annotation { "Feature Type Name" : "Feature", "Feature Type Description" : "" }
export const myFeature = defineFeature(function(context is Context, id is Id, definition is map)
    precondition{}
    {
        {
            var Q0;
            Q0=qCreatedBy(makeId("Top.planeOp"),FACE);
            var sketch = newSketch(context, id + "F0", { "sketchPlane" : qUnion([Q0])});
            skCircle(sketch, "E0", {"center": v(0, 0) * mm, "radius": 50000 * mm});
            skCircle(sketch, "E1", {"center": v(0, 0) * mm, "radius": 40000 * mm});
            skCircle(sketch, "E2", {"center": v(0, 0) * mm, "radius": 30000 * mm});
            skCircle(sketch, "E3", {"center": v(0, 0) * mm, "radius": 20000 * mm});
            skCircle(sketch, "E4", {"center": v(0, 0) * mm, "radius": 10000 * mm});
            skCircle(sketch, "E5", {"center": v(0, 0) * mm, "radius": 8000 * mm});
            skCircle(sketch, "E6", {"center": v(0, 0) * mm, "radius": 6000 * mm});
            skCircle(sketch, "E7", {"center": v(0, 0) * mm, "radius": 4000 * mm});
            skCircle(sketch, "E8", {"center": v(0, 0) * mm, "radius": 2000 * mm});
            skCircle(sketch, "E9.0", {"center": v(0, 0) * mm, "radius": 50100 * mm});
            skCircle(sketch, "E10.0", {"center": v(0, 0) * mm, "radius": 40100 * mm});
            skCircle(sketch, "E11.0", {"center": v(0, 0) * mm, "radius": 30100 * mm});
            skCircle(sketch, "E12.0", {"center": v(0, 0) * mm, "radius": 20100 * mm});
            skCircle(sketch, "E13.0", {"center": v(0, 0) * mm, "radius": 10100 * mm});
            skCircle(sketch, "E14.0", {"center": v(0, 0) * mm, "radius": 8100 * mm});
            skCircle(sketch, "E15.0", {"center": v(0, 0) * mm, "radius": 6100 * mm});
            skCircle(sketch, "E16.0", {"center": v(0, 0) * mm, "radius": 4100 * mm});
            skCircle(sketch, "E17.0", {"center": v(0, 0) * mm, "radius": 2100 * mm});
            skSolve(sketch);
        }
        {
            var Q0;
            Q0=makeQuery(id+"F0.imprint","IMPRINT",FACE,{"disambiguationData":[TD([[makeQuery(id+"F0.imprint","IMPRINT",EDGE,{"derivedFrom":sQuery(id+"F0.wireOp",EDGE,"E0")}),-1.0]])]});
            var Q1;
            Q1=makeQuery(id+"F0.imprint","IMPRINT",FACE,{"disambiguationData":[TD([[makeQuery(id+"F0.imprint","IMPRINT",EDGE,{"derivedFrom":sQuery(id+"F0.wireOp",EDGE,"E1")}),-1.0]])]});
            var Q2;
            Q2=makeQuery(id+"F0.imprint","IMPRINT",FACE,{"disambiguationData":[TD([[makeQuery(id+"F0.imprint","IMPRINT",EDGE,{"derivedFrom":sQuery(id+"F0.wireOp",EDGE,"E2")}),-1.0]])]});
            var Q3;
            Q3=makeQuery(id+"F0.imprint","IMPRINT",FACE,{"disambiguationData":[TD([[makeQuery(id+"F0.imprint","IMPRINT",EDGE,{"derivedFrom":sQuery(id+"F0.wireOp",EDGE,"E3")}),-1.0]])]});
            var Q4;
            Q4=makeQuery(id+"F0.imprint","IMPRINT",FACE,{"disambiguationData":[TD([[makeQuery(id+"F0.imprint","IMPRINT",EDGE,{"derivedFrom":sQuery(id+"F0.wireOp",EDGE,"E4")}),-1.0]])]});
            var Q5;
            Q5=makeQuery(id+"F0.imprint","IMPRINT",FACE,{"disambiguationData":[TD([[makeQuery(id+"F0.imprint","IMPRINT",EDGE,{"derivedFrom":sQuery(id+"F0.wireOp",EDGE,"E5")}),-1.0]])]});
            var Q6;
            Q6=makeQuery(id+"F0.imprint","IMPRINT",FACE,{"disambiguationData":[TD([[makeQuery(id+"F0.imprint","IMPRINT",EDGE,{"derivedFrom":sQuery(id+"F0.wireOp",EDGE,"E6")}),-1.0]])]});
            var Q7;
            Q7=makeQuery(id+"F0.imprint","IMPRINT",FACE,{"disambiguationData":[TD([[makeQuery(id+"F0.imprint","IMPRINT",EDGE,{"derivedFrom":sQuery(id+"F0.wireOp",EDGE,"E7")}),-1.0]])]});
            var Q8;
            Q8=makeQuery(id+"F0.imprint","IMPRINT",FACE,{"disambiguationData":[TD([[makeQuery(id+"F0.imprint","IMPRINT",EDGE,{"derivedFrom":sQuery(id+"F0.wireOp",EDGE,"E8")}),-1.0]])]});
            extrude(context, id + "F1", {"entities" : qUnion([Q0, Q1, Q2, Q3, Q4, Q5, Q6, Q7, Q8]), "depth" : 10 * mm});
        }
        {
            var Q0;
            Q0=qCreatedBy(makeId("Top.planeOp"),FACE);
            var sketch = newSketch(context, id + "F2", { "sketchPlane" : qUnion([Q0])});
            skLineSegment(sketch, "E18.bottom", {"start": v(-15000, 5000) * mm, "end": v(-60000, 5000) * mm});
            skLineSegment(sketch, "E18.top", {"start": v(-15000, -5000) * mm, "end": v(-60000, -5000) * mm});
            skLineSegment(sketch, "E18.left", {"start": v(-15000, 5000) * mm, "end": v(-15000, -5000) * mm});
            skLineSegment(sketch, "E18.right", {"start": v(-60000, 5000) * mm, "end": v(-60000, -5000) * mm});
            skSolve(sketch);
        }
        {
            var Q0;
            Q0=qSketchRegion(id+"F2",true);
            extrude(context, id + "F3", {"entities" : qUnion([Q0]), "operationType" : NewBodyOperationType.REMOVE, "endBound" : BoundingType.THROUGH_ALL, "depth" : 25 * mm});
        }
        {
            var Q0;
            Q0=qCreatedBy(makeId("Top.planeOp"),FACE);
            var sketch = newSketch(context, id + "F4", { "sketchPlane" : qUnion([Q0])});
            skText(sketch, "E19", { "text": "50m", "fontName": "OpenSans-Regular.ttf"});
            skText(sketch, "E20", { "text": "40m", "fontName": "OpenSans-Regular.ttf"});
            skText(sketch, "E21", { "text": "30m", "fontName": "OpenSans-Regular.ttf"});
            skText(sketch, "E22", { "text": "20m", "fontName": "OpenSans-Regular.ttf"});
            const initialGuessF4  = {"E19": [-52.85742, -1, 1, 0, 2], "E20": [-42.85742, -1, 1, 0, 2], "E21": [-32.85742, -1, 1, 0, 2], "E22": [-22.85742, -1, 1, 0, 2]};
            skSetInitialGuess(sketch, initialGuessF4);
            skSolve(sketch);
        }
        {
            var Q0;
            Q0=qSketchRegion(id+"F4",true);
            var Q1;
            Q1=makeQuery(id+"F1.opExtrude","CAP_FACE",FACE,{"disambiguationData":[OSD([sQuery(id+"F0.wireOp",EDGE,"E0"),sQuery(id+"F0.wireOp",EDGE,"E9.0")])],"isStart":false});
            var Q2;
            Q2=makeQuery(id+"F1.opExtrude","SWEPT_BODY",BODY,{"disambiguationData":[OSD([sQuery(id+"F0.wireOp",EDGE,"E0"),sQuery(id+"F0.wireOp",EDGE,"E9.0")])]});
            extrude(context, id + "F5", {"entities" : qUnion([Q0]), "endBound" : BoundingType.UP_TO_SURFACE, "endBoundEntityFace" : qUnion([Q1]), "endBoundEntityBody" : qUnion([Q2]), "depth" : 25 * mm});
        }
        {
            var Q0;
            Q0=qCreatedBy(makeId("Front.planeOp"),FACE);
            var sketch = newSketch(context, id + "F6", { "sketchPlane" : qUnion([Q0])});
            skLineSegment(sketch, "E23", {"start": v(0, 979.96) * mm, "end": v(0, 0) * mm});
            skLineSegment(sketch, "E24", {"start": v(0, 0) * mm, "end": v(1421.91, 0) * mm});
            skSolve(sketch);
        }
        {
            var Q0;
            Q0=makeQuery(id+"F5.opExtrude","SWEPT_BODY",BODY,{"disambiguationData":[OSD([sQuery(id+"F4.wireOp",EDGE,"E22.sketch_text.stroke-20"),sQuery(id+"F4.wireOp",EDGE,"E22.sketch_text.stroke-21"),sQuery(id+"F4.wireOp",EDGE,"E22.sketch_text.stroke-22"),sQuery(id+"F4.wireOp",EDGE,"E22.sketch_text.stroke-23"),sQuery(id+"F4.wireOp",EDGE,"E22.sketch_text.stroke-24"),sQuery(id+"F4.wireOp",EDGE,"E22.sketch_text.stroke-25"),sQuery(id+"F4.wireOp",EDGE,"E22.sketch_text.stroke-26"),sQuery(id+"F4.wireOp",EDGE,"E22.sketch_text.stroke-27"),sQuery(id+"F4.wireOp",EDGE,"E22.sketch_text.stroke-28"),sQuery(id+"F4.wireOp",EDGE,"E22.sketch_text.stroke-29"),sQuery(id+"F4.wireOp",EDGE,"E22.sketch_text.stroke-30"),sQuery(id+"F4.wireOp",EDGE,"E22.sketch_text.stroke-31"),sQuery(id+"F4.wireOp",EDGE,"E22.sketch_text.stroke-32"),sQuery(id+"F4.wireOp",EDGE,"E22.sketch_text.stroke-33"),sQuery(id+"F4.wireOp",EDGE,"E22.sketch_text.stroke-34"),sQuery(id+"F4.wireOp",EDGE,"E22.sketch_text.stroke-35")])]});
            var Q1;
            Q1=makeQuery(id+"F5.opExtrude","SWEPT_BODY",BODY,{"disambiguationData":[OSD([sQuery(id+"F4.wireOp",EDGE,"E22.sketch_text.stroke-0"),sQuery(id+"F4.wireOp",EDGE,"E22.sketch_text.stroke-1"),sQuery(id+"F4.wireOp",EDGE,"E22.sketch_text.stroke-2"),sQuery(id+"F4.wireOp",EDGE,"E22.sketch_text.stroke-3"),sQuery(id+"F4.wireOp",EDGE,"E22.sketch_text.stroke-4"),sQuery(id+"F4.wireOp",EDGE,"E22.sketch_text.stroke-5"),sQuery(id+"F4.wireOp",EDGE,"E22.sketch_text.stroke-6"),sQuery(id+"F4.wireOp",EDGE,"E22.sketch_text.stroke-7"),sQuery(id+"F4.wireOp",EDGE,"E22.sketch_text.stroke-8"),sQuery(id+"F4.wireOp",EDGE,"E22.sketch_text.stroke-9"),sQuery(id+"F4.wireOp",EDGE,"E22.sketch_text.stroke-10"),sQuery(id+"F4.wireOp",EDGE,"E22.sketch_text.stroke-11"),sQuery(id+"F4.wireOp",EDGE,"E22.sketch_text.stroke-12"),sQuery(id+"F4.wireOp",EDGE,"E22.sketch_text.stroke-13"),sQuery(id+"F4.wireOp",EDGE,"E22.sketch_text.stroke-14"),sQuery(id+"F4.wireOp",EDGE,"E22.sketch_text.stroke-15"),sQuery(id+"F4.wireOp",EDGE,"E22.sketch_text.stroke-16"),sQuery(id+"F4.wireOp",EDGE,"E22.sketch_text.stroke-17"),sQuery(id+"F4.wireOp",EDGE,"E22.sketch_text.stroke-18"),sQuery(id+"F4.wireOp",EDGE,"E22.sketch_text.stroke-19")])]});
            var Q2;
            Q2=makeQuery(id+"F5.opExtrude","SWEPT_BODY",BODY,{"disambiguationData":[OSD([sQuery(id+"F4.wireOp",EDGE,"E21.sketch_text.stroke-28"),sQuery(id+"F4.wireOp",EDGE,"E21.sketch_text.stroke-29"),sQuery(id+"F4.wireOp",EDGE,"E21.sketch_text.stroke-30"),sQuery(id+"F4.wireOp",EDGE,"E21.sketch_text.stroke-31"),sQuery(id+"F4.wireOp",EDGE,"E21.sketch_text.stroke-32"),sQuery(id+"F4.wireOp",EDGE,"E21.sketch_text.stroke-33"),sQuery(id+"F4.wireOp",EDGE,"E21.sketch_text.stroke-34"),sQuery(id+"F4.wireOp",EDGE,"E21.sketch_text.stroke-35"),sQuery(id+"F4.wireOp",EDGE,"E21.sketch_text.stroke-36"),sQuery(id+"F4.wireOp",EDGE,"E21.sketch_text.stroke-37"),sQuery(id+"F4.wireOp",EDGE,"E21.sketch_text.stroke-38"),sQuery(id+"F4.wireOp",EDGE,"E21.sketch_text.stroke-39"),sQuery(id+"F4.wireOp",EDGE,"E21.sketch_text.stroke-40"),sQuery(id+"F4.wireOp",EDGE,"E21.sketch_text.stroke-41"),sQuery(id+"F4.wireOp",EDGE,"E21.sketch_text.stroke-42"),sQuery(id+"F4.wireOp",EDGE,"E21.sketch_text.stroke-43")])]});
            var Q3;
            Q3=makeQuery(id+"F5.opExtrude","SWEPT_BODY",BODY,{"disambiguationData":[OSD([sQuery(id+"F4.wireOp",EDGE,"E21.sketch_text.stroke-0"),sQuery(id+"F4.wireOp",EDGE,"E21.sketch_text.stroke-1"),sQuery(id+"F4.wireOp",EDGE,"E21.sketch_text.stroke-2"),sQuery(id+"F4.wireOp",EDGE,"E21.sketch_text.stroke-3"),sQuery(id+"F4.wireOp",EDGE,"E21.sketch_text.stroke-4"),sQuery(id+"F4.wireOp",EDGE,"E21.sketch_text.stroke-5"),sQuery(id+"F4.wireOp",EDGE,"E21.sketch_text.stroke-6"),sQuery(id+"F4.wireOp",EDGE,"E21.sketch_text.stroke-7"),sQuery(id+"F4.wireOp",EDGE,"E21.sketch_text.stroke-8"),sQuery(id+"F4.wireOp",EDGE,"E21.sketch_text.stroke-9"),sQuery(id+"F4.wireOp",EDGE,"E21.sketch_text.stroke-10"),sQuery(id+"F4.wireOp",EDGE,"E21.sketch_text.stroke-11"),sQuery(id+"F4.wireOp",EDGE,"E21.sketch_text.stroke-12"),sQuery(id+"F4.wireOp",EDGE,"E21.sketch_text.stroke-13"),sQuery(id+"F4.wireOp",EDGE,"E21.sketch_text.stroke-14"),sQuery(id+"F4.wireOp",EDGE,"E21.sketch_text.stroke-15"),sQuery(id+"F4.wireOp",EDGE,"E21.sketch_text.stroke-16"),sQuery(id+"F4.wireOp",EDGE,"E21.sketch_text.stroke-17"),sQuery(id+"F4.wireOp",EDGE,"E21.sketch_text.stroke-18"),sQuery(id+"F4.wireOp",EDGE,"E21.sketch_text.stroke-19"),sQuery(id+"F4.wireOp",EDGE,"E21.sketch_text.stroke-20"),sQuery(id+"F4.wireOp",EDGE,"E21.sketch_text.stroke-21"),sQuery(id+"F4.wireOp",EDGE,"E21.sketch_text.stroke-22"),sQuery(id+"F4.wireOp",EDGE,"E21.sketch_text.stroke-23"),sQuery(id+"F4.wireOp",EDGE,"E21.sketch_text.stroke-24"),sQuery(id+"F4.wireOp",EDGE,"E21.sketch_text.stroke-25"),sQuery(id+"F4.wireOp",EDGE,"E21.sketch_text.stroke-26"),sQuery(id+"F4.wireOp",EDGE,"E21.sketch_text.stroke-27")])]});
            var Q4;
            Q4=makeQuery(id+"F5.opExtrude","SWEPT_BODY",BODY,{"disambiguationData":[OSD([sQuery(id+"F4.wireOp",EDGE,"E20.sketch_text.stroke-17"),sQuery(id+"F4.wireOp",EDGE,"E20.sketch_text.stroke-18"),sQuery(id+"F4.wireOp",EDGE,"E20.sketch_text.stroke-19"),sQuery(id+"F4.wireOp",EDGE,"E20.sketch_text.stroke-20"),sQuery(id+"F4.wireOp",EDGE,"E20.sketch_text.stroke-21"),sQuery(id+"F4.wireOp",EDGE,"E20.sketch_text.stroke-22"),sQuery(id+"F4.wireOp",EDGE,"E20.sketch_text.stroke-23"),sQuery(id+"F4.wireOp",EDGE,"E20.sketch_text.stroke-24"),sQuery(id+"F4.wireOp",EDGE,"E20.sketch_text.stroke-25"),sQuery(id+"F4.wireOp",EDGE,"E20.sketch_text.stroke-26"),sQuery(id+"F4.wireOp",EDGE,"E20.sketch_text.stroke-27"),sQuery(id+"F4.wireOp",EDGE,"E20.sketch_text.stroke-28"),sQuery(id+"F4.wireOp",EDGE,"E20.sketch_text.stroke-29"),sQuery(id+"F4.wireOp",EDGE,"E20.sketch_text.stroke-30"),sQuery(id+"F4.wireOp",EDGE,"E20.sketch_text.stroke-31"),sQuery(id+"F4.wireOp",EDGE,"E20.sketch_text.stroke-32")])]});
            var Q5;
            Q5=makeQuery(id+"F5.opExtrude","SWEPT_BODY",BODY,{"disambiguationData":[OSD([sQuery(id+"F4.wireOp",EDGE,"E20.sketch_text.stroke-0"),sQuery(id+"F4.wireOp",EDGE,"E20.sketch_text.stroke-1"),sQuery(id+"F4.wireOp",EDGE,"E20.sketch_text.stroke-2"),sQuery(id+"F4.wireOp",EDGE,"E20.sketch_text.stroke-3"),sQuery(id+"F4.wireOp",EDGE,"E20.sketch_text.stroke-4"),sQuery(id+"F4.wireOp",EDGE,"E20.sketch_text.stroke-5"),sQuery(id+"F4.wireOp",EDGE,"E20.sketch_text.stroke-6"),sQuery(id+"F4.wireOp",EDGE,"E20.sketch_text.stroke-7"),sQuery(id+"F4.wireOp",EDGE,"E20.sketch_text.stroke-8"),sQuery(id+"F4.wireOp",EDGE,"E20.sketch_text.stroke-9"),sQuery(id+"F4.wireOp",EDGE,"E20.sketch_text.stroke-10"),sQuery(id+"F4.wireOp",EDGE,"E20.sketch_text.stroke-11"),sQuery(id+"F4.wireOp",EDGE,"E20.sketch_text.stroke-12"),sQuery(id+"F4.wireOp",EDGE,"E20.sketch_text.stroke-13"),sQuery(id+"F4.wireOp",EDGE,"E20.sketch_text.stroke-14"),sQuery(id+"F4.wireOp",EDGE,"E20.sketch_text.stroke-15"),sQuery(id+"F4.wireOp",EDGE,"E20.sketch_text.stroke-16")])]});
            var Q6;
            Q6=makeQuery(id+"F5.opExtrude","SWEPT_BODY",BODY,{"disambiguationData":[OSD([sQuery(id+"F4.wireOp",EDGE,"E19.sketch_text.stroke-19"),sQuery(id+"F4.wireOp",EDGE,"E19.sketch_text.stroke-20"),sQuery(id+"F4.wireOp",EDGE,"E19.sketch_text.stroke-21"),sQuery(id+"F4.wireOp",EDGE,"E19.sketch_text.stroke-22"),sQuery(id+"F4.wireOp",EDGE,"E19.sketch_text.stroke-23"),sQuery(id+"F4.wireOp",EDGE,"E19.sketch_text.stroke-24"),sQuery(id+"F4.wireOp",EDGE,"E19.sketch_text.stroke-25"),sQuery(id+"F4.wireOp",EDGE,"E19.sketch_text.stroke-26"),sQuery(id+"F4.wireOp",EDGE,"E19.sketch_text.stroke-27"),sQuery(id+"F4.wireOp",EDGE,"E19.sketch_text.stroke-28"),sQuery(id+"F4.wireOp",EDGE,"E19.sketch_text.stroke-29"),sQuery(id+"F4.wireOp",EDGE,"E19.sketch_text.stroke-30"),sQuery(id+"F4.wireOp",EDGE,"E19.sketch_text.stroke-31"),sQuery(id+"F4.wireOp",EDGE,"E19.sketch_text.stroke-32"),sQuery(id+"F4.wireOp",EDGE,"E19.sketch_text.stroke-33"),sQuery(id+"F4.wireOp",EDGE,"E19.sketch_text.stroke-34")])]});
            var Q7;
            Q7=makeQuery(id+"F5.opExtrude","SWEPT_BODY",BODY,{"disambiguationData":[OSD([sQuery(id+"F4.wireOp",EDGE,"E19.sketch_text.stroke-0"),sQuery(id+"F4.wireOp",EDGE,"E19.sketch_text.stroke-1"),sQuery(id+"F4.wireOp",EDGE,"E19.sketch_text.stroke-2"),sQuery(id+"F4.wireOp",EDGE,"E19.sketch_text.stroke-3"),sQuery(id+"F4.wireOp",EDGE,"E19.sketch_text.stroke-4"),sQuery(id+"F4.wireOp",EDGE,"E19.sketch_text.stroke-5"),sQuery(id+"F4.wireOp",EDGE,"E19.sketch_text.stroke-6"),sQuery(id+"F4.wireOp",EDGE,"E19.sketch_text.stroke-7"),sQuery(id+"F4.wireOp",EDGE,"E19.sketch_text.stroke-8"),sQuery(id+"F4.wireOp",EDGE,"E19.sketch_text.stroke-9"),sQuery(id+"F4.wireOp",EDGE,"E19.sketch_text.stroke-10"),sQuery(id+"F4.wireOp",EDGE,"E19.sketch_text.stroke-11"),sQuery(id+"F4.wireOp",EDGE,"E19.sketch_text.stroke-12"),sQuery(id+"F4.wireOp",EDGE,"E19.sketch_text.stroke-13"),sQuery(id+"F4.wireOp",EDGE,"E19.sketch_text.stroke-14"),sQuery(id+"F4.wireOp",EDGE,"E19.sketch_text.stroke-15"),sQuery(id+"F4.wireOp",EDGE,"E19.sketch_text.stroke-16"),sQuery(id+"F4.wireOp",EDGE,"E19.sketch_text.stroke-17"),sQuery(id+"F4.wireOp",EDGE,"E19.sketch_text.stroke-18")])]});
            var Q8;
            Q8=makeQuery(id+"F5.opExtrude","SWEPT_BODY",BODY,{"disambiguationData":[OSD([sQuery(id+"F4.wireOp",EDGE,"E22.sketch_text.stroke-36"),sQuery(id+"F4.wireOp",EDGE,"E22.sketch_text.stroke-37"),sQuery(id+"F4.wireOp",EDGE,"E22.sketch_text.stroke-38"),sQuery(id+"F4.wireOp",EDGE,"E22.sketch_text.stroke-39"),sQuery(id+"F4.wireOp",EDGE,"E22.sketch_text.stroke-40"),sQuery(id+"F4.wireOp",EDGE,"E22.sketch_text.stroke-41"),sQuery(id+"F4.wireOp",EDGE,"E22.sketch_text.stroke-42"),sQuery(id+"F4.wireOp",EDGE,"E22.sketch_text.stroke-43"),sQuery(id+"F4.wireOp",EDGE,"E22.sketch_text.stroke-44"),sQuery(id+"F4.wireOp",EDGE,"E22.sketch_text.stroke-45"),sQuery(id+"F4.wireOp",EDGE,"E22.sketch_text.stroke-46"),sQuery(id+"F4.wireOp",EDGE,"E22.sketch_text.stroke-47"),sQuery(id+"F4.wireOp",EDGE,"E22.sketch_text.stroke-48"),sQuery(id+"F4.wireOp",EDGE,"E22.sketch_text.stroke-49"),sQuery(id+"F4.wireOp",EDGE,"E22.sketch_text.stroke-50"),sQuery(id+"F4.wireOp",EDGE,"E22.sketch_text.stroke-51"),sQuery(id+"F4.wireOp",EDGE,"E22.sketch_text.stroke-52"),sQuery(id+"F4.wireOp",EDGE,"E22.sketch_text.stroke-53"),sQuery(id+"F4.wireOp",EDGE,"E22.sketch_text.stroke-54"),sQuery(id+"F4.wireOp",EDGE,"E22.sketch_text.stroke-55"),sQuery(id+"F4.wireOp",EDGE,"E22.sketch_text.stroke-56"),sQuery(id+"F4.wireOp",EDGE,"E22.sketch_text.stroke-57"),sQuery(id+"F4.wireOp",EDGE,"E22.sketch_text.stroke-58"),sQuery(id+"F4.wireOp",EDGE,"E22.sketch_text.stroke-59"),sQuery(id+"F4.wireOp",EDGE,"E22.sketch_text.stroke-60"),sQuery(id+"F4.wireOp",EDGE,"E22.sketch_text.stroke-61"),sQuery(id+"F4.wireOp",EDGE,"E22.sketch_text.stroke-62"),sQuery(id+"F4.wireOp",EDGE,"E22.sketch_text.stroke-63")])]});
            var Q9;
            Q9=makeQuery(id+"F5.opExtrude","SWEPT_BODY",BODY,{"disambiguationData":[OSD([sQuery(id+"F4.wireOp",EDGE,"E21.sketch_text.stroke-44"),sQuery(id+"F4.wireOp",EDGE,"E21.sketch_text.stroke-45"),sQuery(id+"F4.wireOp",EDGE,"E21.sketch_text.stroke-46"),sQuery(id+"F4.wireOp",EDGE,"E21.sketch_text.stroke-47"),sQuery(id+"F4.wireOp",EDGE,"E21.sketch_text.stroke-48"),sQuery(id+"F4.wireOp",EDGE,"E21.sketch_text.stroke-49"),sQuery(id+"F4.wireOp",EDGE,"E21.sketch_text.stroke-50"),sQuery(id+"F4.wireOp",EDGE,"E21.sketch_text.stroke-51"),sQuery(id+"F4.wireOp",EDGE,"E21.sketch_text.stroke-52"),sQuery(id+"F4.wireOp",EDGE,"E21.sketch_text.stroke-53"),sQuery(id+"F4.wireOp",EDGE,"E21.sketch_text.stroke-54"),sQuery(id+"F4.wireOp",EDGE,"E21.sketch_text.stroke-55"),sQuery(id+"F4.wireOp",EDGE,"E21.sketch_text.stroke-56"),sQuery(id+"F4.wireOp",EDGE,"E21.sketch_text.stroke-57"),sQuery(id+"F4.wireOp",EDGE,"E21.sketch_text.stroke-58"),sQuery(id+"F4.wireOp",EDGE,"E21.sketch_text.stroke-59"),sQuery(id+"F4.wireOp",EDGE,"E21.sketch_text.stroke-60"),sQuery(id+"F4.wireOp",EDGE,"E21.sketch_text.stroke-61"),sQuery(id+"F4.wireOp",EDGE,"E21.sketch_text.stroke-62"),sQuery(id+"F4.wireOp",EDGE,"E21.sketch_text.stroke-63"),sQuery(id+"F4.wireOp",EDGE,"E21.sketch_text.stroke-64"),sQuery(id+"F4.wireOp",EDGE,"E21.sketch_text.stroke-65"),sQuery(id+"F4.wireOp",EDGE,"E21.sketch_text.stroke-66"),sQuery(id+"F4.wireOp",EDGE,"E21.sketch_text.stroke-67"),sQuery(id+"F4.wireOp",EDGE,"E21.sketch_text.stroke-68"),sQuery(id+"F4.wireOp",EDGE,"E21.sketch_text.stroke-69"),sQuery(id+"F4.wireOp",EDGE,"E21.sketch_text.stroke-70"),sQuery(id+"F4.wireOp",EDGE,"E21.sketch_text.stroke-71")])]});
            var Q10;
            Q10=makeQuery(id+"F5.opExtrude","SWEPT_BODY",BODY,{"disambiguationData":[OSD([sQuery(id+"F4.wireOp",EDGE,"E20.sketch_text.stroke-33"),sQuery(id+"F4.wireOp",EDGE,"E20.sketch_text.stroke-34"),sQuery(id+"F4.wireOp",EDGE,"E20.sketch_text.stroke-35"),sQuery(id+"F4.wireOp",EDGE,"E20.sketch_text.stroke-36"),sQuery(id+"F4.wireOp",EDGE,"E20.sketch_text.stroke-37"),sQuery(id+"F4.wireOp",EDGE,"E20.sketch_text.stroke-38"),sQuery(id+"F4.wireOp",EDGE,"E20.sketch_text.stroke-39"),sQuery(id+"F4.wireOp",EDGE,"E20.sketch_text.stroke-40"),sQuery(id+"F4.wireOp",EDGE,"E20.sketch_text.stroke-41"),sQuery(id+"F4.wireOp",EDGE,"E20.sketch_text.stroke-42"),sQuery(id+"F4.wireOp",EDGE,"E20.sketch_text.stroke-43"),sQuery(id+"F4.wireOp",EDGE,"E20.sketch_text.stroke-44"),sQuery(id+"F4.wireOp",EDGE,"E20.sketch_text.stroke-45"),sQuery(id+"F4.wireOp",EDGE,"E20.sketch_text.stroke-46"),sQuery(id+"F4.wireOp",EDGE,"E20.sketch_text.stroke-47"),sQuery(id+"F4.wireOp",EDGE,"E20.sketch_text.stroke-48"),sQuery(id+"F4.wireOp",EDGE,"E20.sketch_text.stroke-49"),sQuery(id+"F4.wireOp",EDGE,"E20.sketch_text.stroke-50"),sQuery(id+"F4.wireOp",EDGE,"E20.sketch_text.stroke-51"),sQuery(id+"F4.wireOp",EDGE,"E20.sketch_text.stroke-52"),sQuery(id+"F4.wireOp",EDGE,"E20.sketch_text.stroke-53"),sQuery(id+"F4.wireOp",EDGE,"E20.sketch_text.stroke-54"),sQuery(id+"F4.wireOp",EDGE,"E20.sketch_text.stroke-55"),sQuery(id+"F4.wireOp",EDGE,"E20.sketch_text.stroke-56"),sQuery(id+"F4.wireOp",EDGE,"E20.sketch_text.stroke-57"),sQuery(id+"F4.wireOp",EDGE,"E20.sketch_text.stroke-58"),sQuery(id+"F4.wireOp",EDGE,"E20.sketch_text.stroke-59"),sQuery(id+"F4.wireOp",EDGE,"E20.sketch_text.stroke-60")])]});
            var Q11;
            Q11=makeQuery(id+"F5.opExtrude","SWEPT_BODY",BODY,{"disambiguationData":[OSD([sQuery(id+"F4.wireOp",EDGE,"E19.sketch_text.stroke-35"),sQuery(id+"F4.wireOp",EDGE,"E19.sketch_text.stroke-36"),sQuery(id+"F4.wireOp",EDGE,"E19.sketch_text.stroke-37"),sQuery(id+"F4.wireOp",EDGE,"E19.sketch_text.stroke-38"),sQuery(id+"F4.wireOp",EDGE,"E19.sketch_text.stroke-39"),sQuery(id+"F4.wireOp",EDGE,"E19.sketch_text.stroke-40"),sQuery(id+"F4.wireOp",EDGE,"E19.sketch_text.stroke-41"),sQuery(id+"F4.wireOp",EDGE,"E19.sketch_text.stroke-42"),sQuery(id+"F4.wireOp",EDGE,"E19.sketch_text.stroke-43"),sQuery(id+"F4.wireOp",EDGE,"E19.sketch_text.stroke-44"),sQuery(id+"F4.wireOp",EDGE,"E19.sketch_text.stroke-45"),sQuery(id+"F4.wireOp",EDGE,"E19.sketch_text.stroke-46"),sQuery(id+"F4.wireOp",EDGE,"E19.sketch_text.stroke-47"),sQuery(id+"F4.wireOp",EDGE,"E19.sketch_text.stroke-48"),sQuery(id+"F4.wireOp",EDGE,"E19.sketch_text.stroke-49"),sQuery(id+"F4.wireOp",EDGE,"E19.sketch_text.stroke-50"),sQuery(id+"F4.wireOp",EDGE,"E19.sketch_text.stroke-51"),sQuery(id+"F4.wireOp",EDGE,"E19.sketch_text.stroke-52"),sQuery(id+"F4.wireOp",EDGE,"E19.sketch_text.stroke-53"),sQuery(id+"F4.wireOp",EDGE,"E19.sketch_text.stroke-54"),sQuery(id+"F4.wireOp",EDGE,"E19.sketch_text.stroke-55"),sQuery(id+"F4.wireOp",EDGE,"E19.sketch_text.stroke-56"),sQuery(id+"F4.wireOp",EDGE,"E19.sketch_text.stroke-57"),sQuery(id+"F4.wireOp",EDGE,"E19.sketch_text.stroke-58"),sQuery(id+"F4.wireOp",EDGE,"E19.sketch_text.stroke-59"),sQuery(id+"F4.wireOp",EDGE,"E19.sketch_text.stroke-60"),sQuery(id+"F4.wireOp",EDGE,"E19.sketch_text.stroke-61"),sQuery(id+"F4.wireOp",EDGE,"E19.sketch_text.stroke-62")])]});
            var Q12;
            Q12=sQuery(id+"F6.wireOp",EDGE,"E24");
            transform(context, id + "F7", {"entities" : qUnion([Q0, Q1, Q2, Q3, Q4, Q5, Q6, Q7, Q8, Q9, Q10, Q11]), "transformType" : TransformType.ROTATION, "transformAxis" : qUnion([Q12]), "angle" : 90 * degree, "makeCopy" : false});
        }
        {
            var Q0;
            Q0=makeQuery(id+"F1.opExtrude","SWEPT_BODY",BODY,{"disambiguationData":[OSD([sQuery(id+"F0.wireOp",EDGE,"E8"),sQuery(id+"F0.wireOp",EDGE,"E17.0")])]});
            var Q1;
            Q1=makeQuery(id+"F1.opExtrude","SWEPT_BODY",BODY,{"disambiguationData":[OSD([sQuery(id+"F0.wireOp",EDGE,"E7"),sQuery(id+"F0.wireOp",EDGE,"E16.0")])]});
            var Q2;
            Q2=makeQuery(id+"F1.opExtrude","SWEPT_BODY",BODY,{"disambiguationData":[OSD([sQuery(id+"F0.wireOp",EDGE,"E6"),sQuery(id+"F0.wireOp",EDGE,"E15.0")])]});
            var Q3;
            Q3=makeQuery(id+"F1.opExtrude","SWEPT_BODY",BODY,{"disambiguationData":[OSD([sQuery(id+"F0.wireOp",EDGE,"E5"),sQuery(id+"F0.wireOp",EDGE,"E14.0")])]});
            var Q4;
            Q4=makeQuery(id+"F1.opExtrude","SWEPT_BODY",BODY,{"disambiguationData":[OSD([sQuery(id+"F0.wireOp",EDGE,"E4"),sQuery(id+"F0.wireOp",EDGE,"E13.0")])]});
            var Q5;
            Q5=makeQuery(id+"F1.opExtrude","SWEPT_BODY",BODY,{"disambiguationData":[OSD([sQuery(id+"F0.wireOp",EDGE,"E3"),sQuery(id+"F0.wireOp",EDGE,"E12.0")])]});
            var Q6;
            Q6=makeQuery(id+"F1.opExtrude","SWEPT_BODY",BODY,{"disambiguationData":[OSD([sQuery(id+"F0.wireOp",EDGE,"E2"),sQuery(id+"F0.wireOp",EDGE,"E11.0")])]});
            var Q7;
            Q7=makeQuery(id+"F1.opExtrude","SWEPT_BODY",BODY,{"disambiguationData":[OSD([sQuery(id+"F0.wireOp",EDGE,"E1"),sQuery(id+"F0.wireOp",EDGE,"E10.0")])]});
            var Q8;
            Q8=makeQuery(id+"F1.opExtrude","SWEPT_BODY",BODY,{"disambiguationData":[OSD([sQuery(id+"F0.wireOp",EDGE,"E0"),sQuery(id+"F0.wireOp",EDGE,"E9.0")])]});
            var Q9;
            Q9=makeQuery(id+"F5.opExtrude","SWEPT_BODY",BODY,{"disambiguationData":[OSD([sQuery(id+"F4.wireOp",EDGE,"E22.sketch_text.stroke-20"),sQuery(id+"F4.wireOp",EDGE,"E22.sketch_text.stroke-21"),sQuery(id+"F4.wireOp",EDGE,"E22.sketch_text.stroke-22"),sQuery(id+"F4.wireOp",EDGE,"E22.sketch_text.stroke-23"),sQuery(id+"F4.wireOp",EDGE,"E22.sketch_text.stroke-24"),sQuery(id+"F4.wireOp",EDGE,"E22.sketch_text.stroke-25"),sQuery(id+"F4.wireOp",EDGE,"E22.sketch_text.stroke-26"),sQuery(id+"F4.wireOp",EDGE,"E22.sketch_text.stroke-27"),sQuery(id+"F4.wireOp",EDGE,"E22.sketch_text.stroke-28"),sQuery(id+"F4.wireOp",EDGE,"E22.sketch_text.stroke-29"),sQuery(id+"F4.wireOp",EDGE,"E22.sketch_text.stroke-30"),sQuery(id+"F4.wireOp",EDGE,"E22.sketch_text.stroke-31"),sQuery(id+"F4.wireOp",EDGE,"E22.sketch_text.stroke-32"),sQuery(id+"F4.wireOp",EDGE,"E22.sketch_text.stroke-33"),sQuery(id+"F4.wireOp",EDGE,"E22.sketch_text.stroke-34"),sQuery(id+"F4.wireOp",EDGE,"E22.sketch_text.stroke-35")])]});
            var Q10;
            Q10=makeQuery(id+"F5.opExtrude","SWEPT_BODY",BODY,{"disambiguationData":[OSD([sQuery(id+"F4.wireOp",EDGE,"E22.sketch_text.stroke-0"),sQuery(id+"F4.wireOp",EDGE,"E22.sketch_text.stroke-1"),sQuery(id+"F4.wireOp",EDGE,"E22.sketch_text.stroke-2"),sQuery(id+"F4.wireOp",EDGE,"E22.sketch_text.stroke-3"),sQuery(id+"F4.wireOp",EDGE,"E22.sketch_text.stroke-4"),sQuery(id+"F4.wireOp",EDGE,"E22.sketch_text.stroke-5"),sQuery(id+"F4.wireOp",EDGE,"E22.sketch_text.stroke-6"),sQuery(id+"F4.wireOp",EDGE,"E22.sketch_text.stroke-7"),sQuery(id+"F4.wireOp",EDGE,"E22.sketch_text.stroke-8"),sQuery(id+"F4.wireOp",EDGE,"E22.sketch_text.stroke-9"),sQuery(id+"F4.wireOp",EDGE,"E22.sketch_text.stroke-10"),sQuery(id+"F4.wireOp",EDGE,"E22.sketch_text.stroke-11"),sQuery(id+"F4.wireOp",EDGE,"E22.sketch_text.stroke-12"),sQuery(id+"F4.wireOp",EDGE,"E22.sketch_text.stroke-13"),sQuery(id+"F4.wireOp",EDGE,"E22.sketch_text.stroke-14"),sQuery(id+"F4.wireOp",EDGE,"E22.sketch_text.stroke-15"),sQuery(id+"F4.wireOp",EDGE,"E22.sketch_text.stroke-16"),sQuery(id+"F4.wireOp",EDGE,"E22.sketch_text.stroke-17"),sQuery(id+"F4.wireOp",EDGE,"E22.sketch_text.stroke-18"),sQuery(id+"F4.wireOp",EDGE,"E22.sketch_text.stroke-19")])]});
            var Q11;
            Q11=makeQuery(id+"F5.opExtrude","SWEPT_BODY",BODY,{"disambiguationData":[OSD([sQuery(id+"F4.wireOp",EDGE,"E21.sketch_text.stroke-28"),sQuery(id+"F4.wireOp",EDGE,"E21.sketch_text.stroke-29"),sQuery(id+"F4.wireOp",EDGE,"E21.sketch_text.stroke-30"),sQuery(id+"F4.wireOp",EDGE,"E21.sketch_text.stroke-31"),sQuery(id+"F4.wireOp",EDGE,"E21.sketch_text.stroke-32"),sQuery(id+"F4.wireOp",EDGE,"E21.sketch_text.stroke-33"),sQuery(id+"F4.wireOp",EDGE,"E21.sketch_text.stroke-34"),sQuery(id+"F4.wireOp",EDGE,"E21.sketch_text.stroke-35"),sQuery(id+"F4.wireOp",EDGE,"E21.sketch_text.stroke-36"),sQuery(id+"F4.wireOp",EDGE,"E21.sketch_text.stroke-37"),sQuery(id+"F4.wireOp",EDGE,"E21.sketch_text.stroke-38"),sQuery(id+"F4.wireOp",EDGE,"E21.sketch_text.stroke-39"),sQuery(id+"F4.wireOp",EDGE,"E21.sketch_text.stroke-40"),sQuery(id+"F4.wireOp",EDGE,"E21.sketch_text.stroke-41"),sQuery(id+"F4.wireOp",EDGE,"E21.sketch_text.stroke-42"),sQuery(id+"F4.wireOp",EDGE,"E21.sketch_text.stroke-43")])]});
            var Q12;
            Q12=makeQuery(id+"F5.opExtrude","SWEPT_BODY",BODY,{"disambiguationData":[OSD([sQuery(id+"F4.wireOp",EDGE,"E21.sketch_text.stroke-0"),sQuery(id+"F4.wireOp",EDGE,"E21.sketch_text.stroke-1"),sQuery(id+"F4.wireOp",EDGE,"E21.sketch_text.stroke-2"),sQuery(id+"F4.wireOp",EDGE,"E21.sketch_text.stroke-3"),sQuery(id+"F4.wireOp",EDGE,"E21.sketch_text.stroke-4"),sQuery(id+"F4.wireOp",EDGE,"E21.sketch_text.stroke-5"),sQuery(id+"F4.wireOp",EDGE,"E21.sketch_text.stroke-6"),sQuery(id+"F4.wireOp",EDGE,"E21.sketch_text.stroke-7"),sQuery(id+"F4.wireOp",EDGE,"E21.sketch_text.stroke-8"),sQuery(id+"F4.wireOp",EDGE,"E21.sketch_text.stroke-9"),sQuery(id+"F4.wireOp",EDGE,"E21.sketch_text.stroke-10"),sQuery(id+"F4.wireOp",EDGE,"E21.sketch_text.stroke-11"),sQuery(id+"F4.wireOp",EDGE,"E21.sketch_text.stroke-12"),sQuery(id+"F4.wireOp",EDGE,"E21.sketch_text.stroke-13"),sQuery(id+"F4.wireOp",EDGE,"E21.sketch_text.stroke-14"),sQuery(id+"F4.wireOp",EDGE,"E21.sketch_text.stroke-15"),sQuery(id+"F4.wireOp",EDGE,"E21.sketch_text.stroke-16"),sQuery(id+"F4.wireOp",EDGE,"E21.sketch_text.stroke-17"),sQuery(id+"F4.wireOp",EDGE,"E21.sketch_text.stroke-18"),sQuery(id+"F4.wireOp",EDGE,"E21.sketch_text.stroke-19"),sQuery(id+"F4.wireOp",EDGE,"E21.sketch_text.stroke-20"),sQuery(id+"F4.wireOp",EDGE,"E21.sketch_text.stroke-21"),sQuery(id+"F4.wireOp",EDGE,"E21.sketch_text.stroke-22"),sQuery(id+"F4.wireOp",EDGE,"E21.sketch_text.stroke-23"),sQuery(id+"F4.wireOp",EDGE,"E21.sketch_text.stroke-24"),sQuery(id+"F4.wireOp",EDGE,"E21.sketch_text.stroke-25"),sQuery(id+"F4.wireOp",EDGE,"E21.sketch_text.stroke-26"),sQuery(id+"F4.wireOp",EDGE,"E21.sketch_text.stroke-27")])]});
            var Q13;
            Q13=makeQuery(id+"F5.opExtrude","SWEPT_BODY",BODY,{"disambiguationData":[OSD([sQuery(id+"F4.wireOp",EDGE,"E20.sketch_text.stroke-17"),sQuery(id+"F4.wireOp",EDGE,"E20.sketch_text.stroke-18"),sQuery(id+"F4.wireOp",EDGE,"E20.sketch_text.stroke-19"),sQuery(id+"F4.wireOp",EDGE,"E20.sketch_text.stroke-20"),sQuery(id+"F4.wireOp",EDGE,"E20.sketch_text.stroke-21"),sQuery(id+"F4.wireOp",EDGE,"E20.sketch_text.stroke-22"),sQuery(id+"F4.wireOp",EDGE,"E20.sketch_text.stroke-23"),sQuery(id+"F4.wireOp",EDGE,"E20.sketch_text.stroke-24"),sQuery(id+"F4.wireOp",EDGE,"E20.sketch_text.stroke-25"),sQuery(id+"F4.wireOp",EDGE,"E20.sketch_text.stroke-26"),sQuery(id+"F4.wireOp",EDGE,"E20.sketch_text.stroke-27"),sQuery(id+"F4.wireOp",EDGE,"E20.sketch_text.stroke-28"),sQuery(id+"F4.wireOp",EDGE,"E20.sketch_text.stroke-29"),sQuery(id+"F4.wireOp",EDGE,"E20.sketch_text.stroke-30"),sQuery(id+"F4.wireOp",EDGE,"E20.sketch_text.stroke-31"),sQuery(id+"F4.wireOp",EDGE,"E20.sketch_text.stroke-32")])]});
            var Q14;
            Q14=makeQuery(id+"F5.opExtrude","SWEPT_BODY",BODY,{"disambiguationData":[OSD([sQuery(id+"F4.wireOp",EDGE,"E20.sketch_text.stroke-0"),sQuery(id+"F4.wireOp",EDGE,"E20.sketch_text.stroke-1"),sQuery(id+"F4.wireOp",EDGE,"E20.sketch_text.stroke-2"),sQuery(id+"F4.wireOp",EDGE,"E20.sketch_text.stroke-3"),sQuery(id+"F4.wireOp",EDGE,"E20.sketch_text.stroke-4"),sQuery(id+"F4.wireOp",EDGE,"E20.sketch_text.stroke-5"),sQuery(id+"F4.wireOp",EDGE,"E20.sketch_text.stroke-6"),sQuery(id+"F4.wireOp",EDGE,"E20.sketch_text.stroke-7"),sQuery(id+"F4.wireOp",EDGE,"E20.sketch_text.stroke-8"),sQuery(id+"F4.wireOp",EDGE,"E20.sketch_text.stroke-9"),sQuery(id+"F4.wireOp",EDGE,"E20.sketch_text.stroke-10"),sQuery(id+"F4.wireOp",EDGE,"E20.sketch_text.stroke-11"),sQuery(id+"F4.wireOp",EDGE,"E20.sketch_text.stroke-12"),sQuery(id+"F4.wireOp",EDGE,"E20.sketch_text.stroke-13"),sQuery(id+"F4.wireOp",EDGE,"E20.sketch_text.stroke-14"),sQuery(id+"F4.wireOp",EDGE,"E20.sketch_text.stroke-15"),sQuery(id+"F4.wireOp",EDGE,"E20.sketch_text.stroke-16")])]});
            var Q15;
            Q15=makeQuery(id+"F5.opExtrude","SWEPT_BODY",BODY,{"disambiguationData":[OSD([sQuery(id+"F4.wireOp",EDGE,"E19.sketch_text.stroke-19"),sQuery(id+"F4.wireOp",EDGE,"E19.sketch_text.stroke-20"),sQuery(id+"F4.wireOp",EDGE,"E19.sketch_text.stroke-21"),sQuery(id+"F4.wireOp",EDGE,"E19.sketch_text.stroke-22"),sQuery(id+"F4.wireOp",EDGE,"E19.sketch_text.stroke-23"),sQuery(id+"F4.wireOp",EDGE,"E19.sketch_text.stroke-24"),sQuery(id+"F4.wireOp",EDGE,"E19.sketch_text.stroke-25"),sQuery(id+"F4.wireOp",EDGE,"E19.sketch_text.stroke-26"),sQuery(id+"F4.wireOp",EDGE,"E19.sketch_text.stroke-27"),sQuery(id+"F4.wireOp",EDGE,"E19.sketch_text.stroke-28"),sQuery(id+"F4.wireOp",EDGE,"E19.sketch_text.stroke-29"),sQuery(id+"F4.wireOp",EDGE,"E19.sketch_text.stroke-30"),sQuery(id+"F4.wireOp",EDGE,"E19.sketch_text.stroke-31"),sQuery(id+"F4.wireOp",EDGE,"E19.sketch_text.stroke-32"),sQuery(id+"F4.wireOp",EDGE,"E19.sketch_text.stroke-33"),sQuery(id+"F4.wireOp",EDGE,"E19.sketch_text.stroke-34")])]});
            var Q16;
            Q16=makeQuery(id+"F5.opExtrude","SWEPT_BODY",BODY,{"disambiguationData":[OSD([sQuery(id+"F4.wireOp",EDGE,"E19.sketch_text.stroke-0"),sQuery(id+"F4.wireOp",EDGE,"E19.sketch_text.stroke-1"),sQuery(id+"F4.wireOp",EDGE,"E19.sketch_text.stroke-2"),sQuery(id+"F4.wireOp",EDGE,"E19.sketch_text.stroke-3"),sQuery(id+"F4.wireOp",EDGE,"E19.sketch_text.stroke-4"),sQuery(id+"F4.wireOp",EDGE,"E19.sketch_text.stroke-5"),sQuery(id+"F4.wireOp",EDGE,"E19.sketch_text.stroke-6"),sQuery(id+"F4.wireOp",EDGE,"E19.sketch_text.stroke-7"),sQuery(id+"F4.wireOp",EDGE,"E19.sketch_text.stroke-8"),sQuery(id+"F4.wireOp",EDGE,"E19.sketch_text.stroke-9"),sQuery(id+"F4.wireOp",EDGE,"E19.sketch_text.stroke-10"),sQuery(id+"F4.wireOp",EDGE,"E19.sketch_text.stroke-11"),sQuery(id+"F4.wireOp",EDGE,"E19.sketch_text.stroke-12"),sQuery(id+"F4.wireOp",EDGE,"E19.sketch_text.stroke-13"),sQuery(id+"F4.wireOp",EDGE,"E19.sketch_text.stroke-14"),sQuery(id+"F4.wireOp",EDGE,"E19.sketch_text.stroke-15"),sQuery(id+"F4.wireOp",EDGE,"E19.sketch_text.stroke-16"),sQuery(id+"F4.wireOp",EDGE,"E19.sketch_text.stroke-17"),sQuery(id+"F4.wireOp",EDGE,"E19.sketch_text.stroke-18")])]});
            var Q17;
            Q17=makeQuery(id+"F5.opExtrude","SWEPT_BODY",BODY,{"disambiguationData":[OSD([sQuery(id+"F4.wireOp",EDGE,"E22.sketch_text.stroke-36"),sQuery(id+"F4.wireOp",EDGE,"E22.sketch_text.stroke-37"),sQuery(id+"F4.wireOp",EDGE,"E22.sketch_text.stroke-38"),sQuery(id+"F4.wireOp",EDGE,"E22.sketch_text.stroke-39"),sQuery(id+"F4.wireOp",EDGE,"E22.sketch_text.stroke-40"),sQuery(id+"F4.wireOp",EDGE,"E22.sketch_text.stroke-41"),sQuery(id+"F4.wireOp",EDGE,"E22.sketch_text.stroke-42"),sQuery(id+"F4.wireOp",EDGE,"E22.sketch_text.stroke-43"),sQuery(id+"F4.wireOp",EDGE,"E22.sketch_text.stroke-44"),sQuery(id+"F4.wireOp",EDGE,"E22.sketch_text.stroke-45"),sQuery(id+"F4.wireOp",EDGE,"E22.sketch_text.stroke-46"),sQuery(id+"F4.wireOp",EDGE,"E22.sketch_text.stroke-47"),sQuery(id+"F4.wireOp",EDGE,"E22.sketch_text.stroke-48"),sQuery(id+"F4.wireOp",EDGE,"E22.sketch_text.stroke-49"),sQuery(id+"F4.wireOp",EDGE,"E22.sketch_text.stroke-50"),sQuery(id+"F4.wireOp",EDGE,"E22.sketch_text.stroke-51"),sQuery(id+"F4.wireOp",EDGE,"E22.sketch_text.stroke-52"),sQuery(id+"F4.wireOp",EDGE,"E22.sketch_text.stroke-53"),sQuery(id+"F4.wireOp",EDGE,"E22.sketch_text.stroke-54"),sQuery(id+"F4.wireOp",EDGE,"E22.sketch_text.stroke-55"),sQuery(id+"F4.wireOp",EDGE,"E22.sketch_text.stroke-56"),sQuery(id+"F4.wireOp",EDGE,"E22.sketch_text.stroke-57"),sQuery(id+"F4.wireOp",EDGE,"E22.sketch_text.stroke-58"),sQuery(id+"F4.wireOp",EDGE,"E22.sketch_text.stroke-59"),sQuery(id+"F4.wireOp",EDGE,"E22.sketch_text.stroke-60"),sQuery(id+"F4.wireOp",EDGE,"E22.sketch_text.stroke-61"),sQuery(id+"F4.wireOp",EDGE,"E22.sketch_text.stroke-62"),sQuery(id+"F4.wireOp",EDGE,"E22.sketch_text.stroke-63")])]});
            var Q18;
            Q18=makeQuery(id+"F5.opExtrude","SWEPT_BODY",BODY,{"disambiguationData":[OSD([sQuery(id+"F4.wireOp",EDGE,"E21.sketch_text.stroke-44"),sQuery(id+"F4.wireOp",EDGE,"E21.sketch_text.stroke-45"),sQuery(id+"F4.wireOp",EDGE,"E21.sketch_text.stroke-46"),sQuery(id+"F4.wireOp",EDGE,"E21.sketch_text.stroke-47"),sQuery(id+"F4.wireOp",EDGE,"E21.sketch_text.stroke-48"),sQuery(id+"F4.wireOp",EDGE,"E21.sketch_text.stroke-49"),sQuery(id+"F4.wireOp",EDGE,"E21.sketch_text.stroke-50"),sQuery(id+"F4.wireOp",EDGE,"E21.sketch_text.stroke-51"),sQuery(id+"F4.wireOp",EDGE,"E21.sketch_text.stroke-52"),sQuery(id+"F4.wireOp",EDGE,"E21.sketch_text.stroke-53"),sQuery(id+"F4.wireOp",EDGE,"E21.sketch_text.stroke-54"),sQuery(id+"F4.wireOp",EDGE,"E21.sketch_text.stroke-55"),sQuery(id+"F4.wireOp",EDGE,"E21.sketch_text.stroke-56"),sQuery(id+"F4.wireOp",EDGE,"E21.sketch_text.stroke-57"),sQuery(id+"F4.wireOp",EDGE,"E21.sketch_text.stroke-58"),sQuery(id+"F4.wireOp",EDGE,"E21.sketch_text.stroke-59"),sQuery(id+"F4.wireOp",EDGE,"E21.sketch_text.stroke-60"),sQuery(id+"F4.wireOp",EDGE,"E21.sketch_text.stroke-61"),sQuery(id+"F4.wireOp",EDGE,"E21.sketch_text.stroke-62"),sQuery(id+"F4.wireOp",EDGE,"E21.sketch_text.stroke-63"),sQuery(id+"F4.wireOp",EDGE,"E21.sketch_text.stroke-64"),sQuery(id+"F4.wireOp",EDGE,"E21.sketch_text.stroke-65"),sQuery(id+"F4.wireOp",EDGE,"E21.sketch_text.stroke-66"),sQuery(id+"F4.wireOp",EDGE,"E21.sketch_text.stroke-67"),sQuery(id+"F4.wireOp",EDGE,"E21.sketch_text.stroke-68"),sQuery(id+"F4.wireOp",EDGE,"E21.sketch_text.stroke-69"),sQuery(id+"F4.wireOp",EDGE,"E21.sketch_text.stroke-70"),sQuery(id+"F4.wireOp",EDGE,"E21.sketch_text.stroke-71")])]});
            var Q19;
            Q19=makeQuery(id+"F5.opExtrude","SWEPT_BODY",BODY,{"disambiguationData":[OSD([sQuery(id+"F4.wireOp",EDGE,"E20.sketch_text.stroke-33"),sQuery(id+"F4.wireOp",EDGE,"E20.sketch_text.stroke-34"),sQuery(id+"F4.wireOp",EDGE,"E20.sketch_text.stroke-35"),sQuery(id+"F4.wireOp",EDGE,"E20.sketch_text.stroke-36"),sQuery(id+"F4.wireOp",EDGE,"E20.sketch_text.stroke-37"),sQuery(id+"F4.wireOp",EDGE,"E20.sketch_text.stroke-38"),sQuery(id+"F4.wireOp",EDGE,"E20.sketch_text.stroke-39"),sQuery(id+"F4.wireOp",EDGE,"E20.sketch_text.stroke-40"),sQuery(id+"F4.wireOp",EDGE,"E20.sketch_text.stroke-41"),sQuery(id+"F4.wireOp",EDGE,"E20.sketch_text.stroke-42"),sQuery(id+"F4.wireOp",EDGE,"E20.sketch_text.stroke-43"),sQuery(id+"F4.wireOp",EDGE,"E20.sketch_text.stroke-44"),sQuery(id+"F4.wireOp",EDGE,"E20.sketch_text.stroke-45"),sQuery(id+"F4.wireOp",EDGE,"E20.sketch_text.stroke-46"),sQuery(id+"F4.wireOp",EDGE,"E20.sketch_text.stroke-47"),sQuery(id+"F4.wireOp",EDGE,"E20.sketch_text.stroke-48"),sQuery(id+"F4.wireOp",EDGE,"E20.sketch_text.stroke-49"),sQuery(id+"F4.wireOp",EDGE,"E20.sketch_text.stroke-50"),sQuery(id+"F4.wireOp",EDGE,"E20.sketch_text.stroke-51"),sQuery(id+"F4.wireOp",EDGE,"E20.sketch_text.stroke-52"),sQuery(id+"F4.wireOp",EDGE,"E20.sketch_text.stroke-53"),sQuery(id+"F4.wireOp",EDGE,"E20.sketch_text.stroke-54"),sQuery(id+"F4.wireOp",EDGE,"E20.sketch_text.stroke-55"),sQuery(id+"F4.wireOp",EDGE,"E20.sketch_text.stroke-56"),sQuery(id+"F4.wireOp",EDGE,"E20.sketch_text.stroke-57"),sQuery(id+"F4.wireOp",EDGE,"E20.sketch_text.stroke-58"),sQuery(id+"F4.wireOp",EDGE,"E20.sketch_text.stroke-59"),sQuery(id+"F4.wireOp",EDGE,"E20.sketch_text.stroke-60")])]});
            var Q20;
            Q20=makeQuery(id+"F5.opExtrude","SWEPT_BODY",BODY,{"disambiguationData":[OSD([sQuery(id+"F4.wireOp",EDGE,"E19.sketch_text.stroke-35"),sQuery(id+"F4.wireOp",EDGE,"E19.sketch_text.stroke-36"),sQuery(id+"F4.wireOp",EDGE,"E19.sketch_text.stroke-37"),sQuery(id+"F4.wireOp",EDGE,"E19.sketch_text.stroke-38"),sQuery(id+"F4.wireOp",EDGE,"E19.sketch_text.stroke-39"),sQuery(id+"F4.wireOp",EDGE,"E19.sketch_text.stroke-40"),sQuery(id+"F4.wireOp",EDGE,"E19.sketch_text.stroke-41"),sQuery(id+"F4.wireOp",EDGE,"E19.sketch_text.stroke-42"),sQuery(id+"F4.wireOp",EDGE,"E19.sketch_text.stroke-43"),sQuery(id+"F4.wireOp",EDGE,"E19.sketch_text.stroke-44"),sQuery(id+"F4.wireOp",EDGE,"E19.sketch_text.stroke-45"),sQuery(id+"F4.wireOp",EDGE,"E19.sketch_text.stroke-46"),sQuery(id+"F4.wireOp",EDGE,"E19.sketch_text.stroke-47"),sQuery(id+"F4.wireOp",EDGE,"E19.sketch_text.stroke-48"),sQuery(id+"F4.wireOp",EDGE,"E19.sketch_text.stroke-49"),sQuery(id+"F4.wireOp",EDGE,"E19.sketch_text.stroke-50"),sQuery(id+"F4.wireOp",EDGE,"E19.sketch_text.stroke-51"),sQuery(id+"F4.wireOp",EDGE,"E19.sketch_text.stroke-52"),sQuery(id+"F4.wireOp",EDGE,"E19.sketch_text.stroke-53"),sQuery(id+"F4.wireOp",EDGE,"E19.sketch_text.stroke-54"),sQuery(id+"F4.wireOp",EDGE,"E19.sketch_text.stroke-55"),sQuery(id+"F4.wireOp",EDGE,"E19.sketch_text.stroke-56"),sQuery(id+"F4.wireOp",EDGE,"E19.sketch_text.stroke-57"),sQuery(id+"F4.wireOp",EDGE,"E19.sketch_text.stroke-58"),sQuery(id+"F4.wireOp",EDGE,"E19.sketch_text.stroke-59"),sQuery(id+"F4.wireOp",EDGE,"E19.sketch_text.stroke-60"),sQuery(id+"F4.wireOp",EDGE,"E19.sketch_text.stroke-61"),sQuery(id+"F4.wireOp",EDGE,"E19.sketch_text.stroke-62")])]});
            var Q21;
            Q21=sQuery(id+"F6.wireOp",EDGE,"E24");
            transform(context, id + "F8", {"entities" : qUnion([Q0, Q1, Q2, Q3, Q4, Q5, Q6, Q7, Q8, Q9, Q10, Q11, Q12, Q13, Q14, Q15, Q16, Q17, Q18, Q19, Q20]), "transformType" : TransformType.ROTATION, "transformAxis" : qUnion([Q21]), "angle" : 20 * degree, "makeCopy" : false});
        }
    });